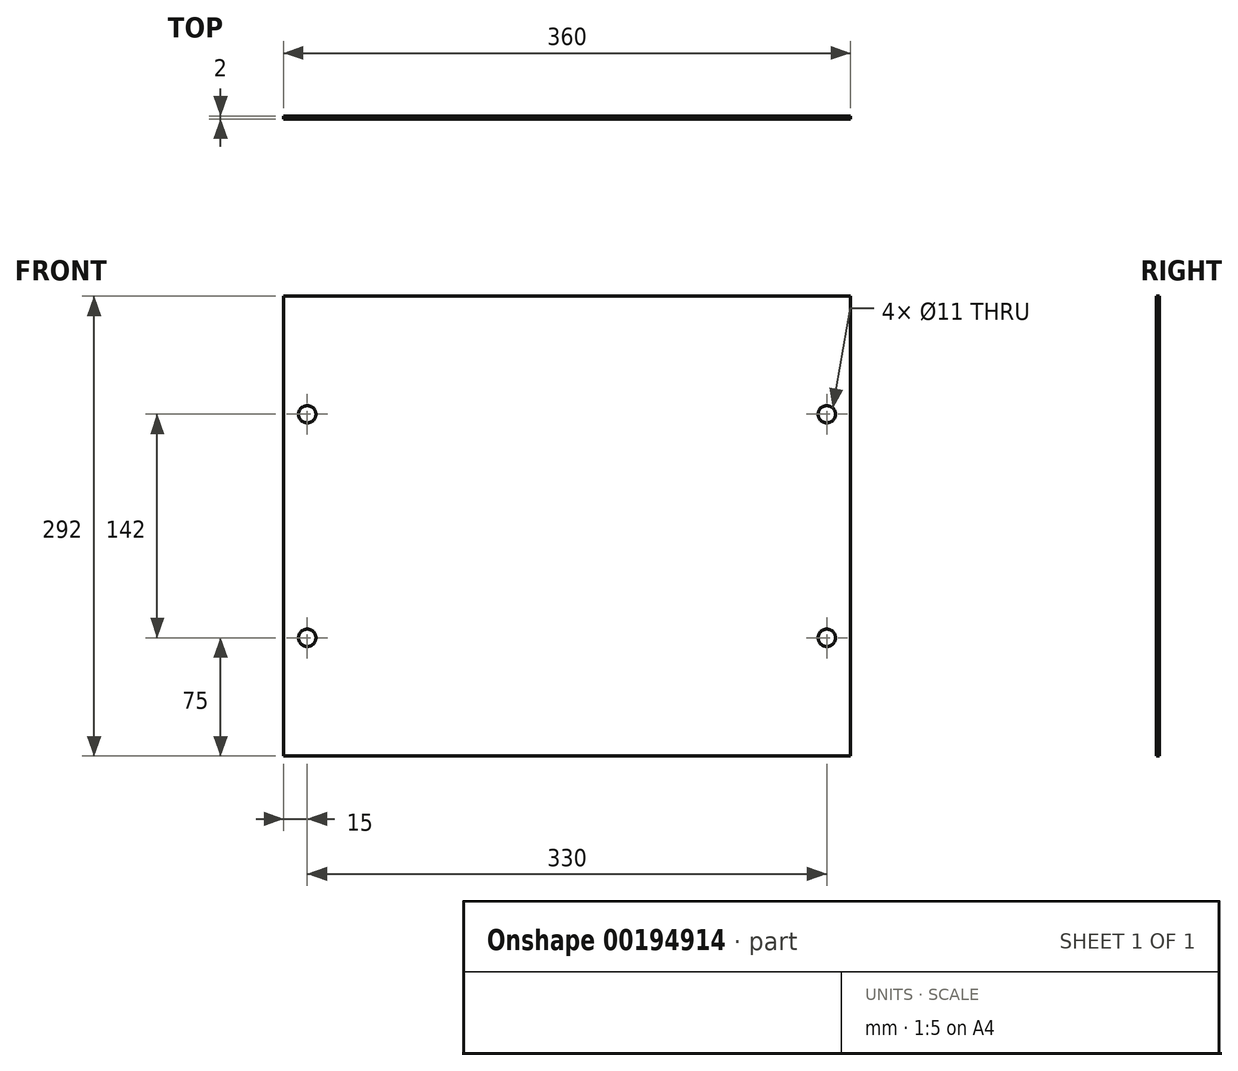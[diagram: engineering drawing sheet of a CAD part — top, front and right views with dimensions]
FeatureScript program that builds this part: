
annotation { "Feature Type Name" : "Feature", "Feature Type Description" : "" }
export const myFeature = defineFeature(function(context is Context, id is Id, definition is map)
    precondition{}
    {
        {
            var Q0;
            Q0=qCreatedBy(makeId("Front.planeOp"),FACE);
            var sketch = newSketch(context, id + "F0", { "sketchPlane" : qUnion([Q0])});
            skLineSegment(sketch, "E0.bottom", {"start": v(0, 0) * mm, "end": v(360, 0) * mm});
            skLineSegment(sketch, "E0.top", {"start": v(0, 292) * mm, "end": v(360, 292) * mm});
            skLineSegment(sketch, "E0.left", {"start": v(0, 0) * mm, "end": v(0, 292) * mm});
            skLineSegment(sketch, "E0.right", {"start": v(360, 0) * mm, "end": v(360, 292) * mm});
            skCircle(sketch, "E1", {"center": v(15, 75) * mm, "radius": 5.5 * mm});
            skCircle(sketch, "E2", {"center": v(345, 75) * mm, "radius": 5.5 * mm});
            skCircle(sketch, "E3", {"center": v(345, 217) * mm, "radius": 5.5 * mm});
            skCircle(sketch, "E4", {"center": v(15, 217) * mm, "radius": 5.5 * mm});
            skSolve(sketch);
        }
        {
            var Q0;
            Q0 = qSketchRegion(id + "F0", true);
            extrude(context, id + "F1", {"entities" : qUnion([Q0]), "depth" : 2 * mm});
        }
    });
